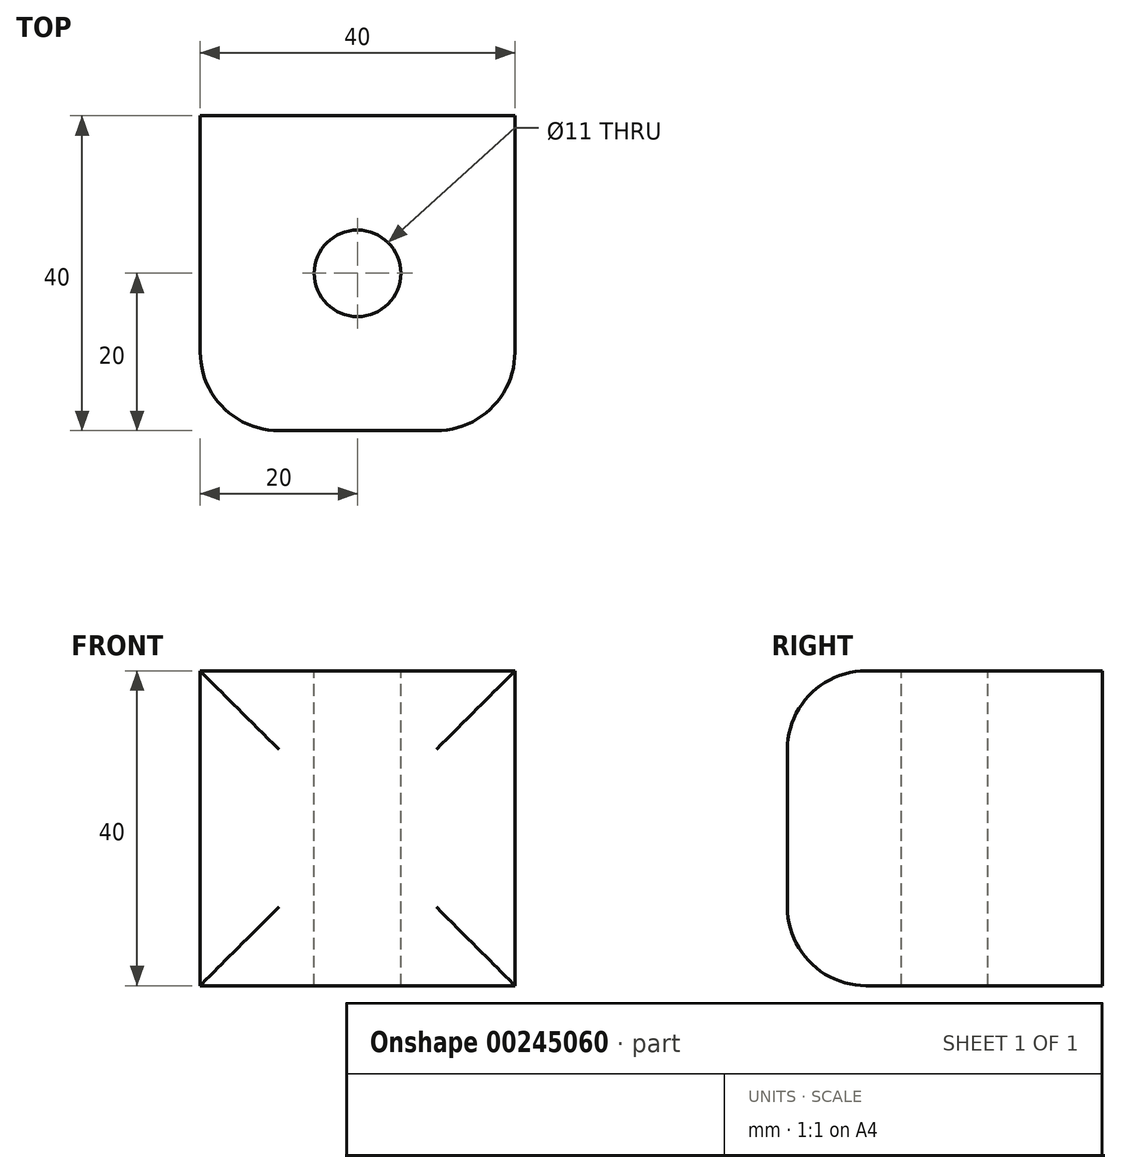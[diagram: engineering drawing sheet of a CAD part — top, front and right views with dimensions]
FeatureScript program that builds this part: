
annotation { "Feature Type Name" : "Feature", "Feature Type Description" : "" }
export const myFeature = defineFeature(function(context is Context, id is Id, definition is map)
    precondition{}
    {
        {
            var Q0;
            Q0=qCreatedBy(makeId("Top.planeOp"),FACE);
            var sketch = newSketch(context, id + "F0", { "sketchPlane" : qUnion([Q0])});
            skLineSegment(sketch, "E0.bottom", {"start": v(-20, 20) * mm, "end": v(20, 20) * mm});
            skLineSegment(sketch, "E0.top", {"start": v(-20, -20) * mm, "end": v(20, -20) * mm});
            skLineSegment(sketch, "E0.left", {"start": v(-20, 20) * mm, "end": v(-20, -20) * mm});
            skLineSegment(sketch, "E0.right", {"start": v(20, 20) * mm, "end": v(20, -20) * mm});
            skPoint(sketch, "E0.middle", {"position": v(0, 0) * mm});
            skSolve(sketch);
        }
        {
            var Q0;
            Q0 = qSketchRegion(id + "F0", true);
            extrude(context, id + "F1", {"entities" : qUnion([Q0]), "depth" : 20 * mm, "hasSecondDirection" : true, "secondDirectionOppositeDirection" : true, "secondDirectionDepth" : 20 * mm});
        }
        {
            var Q0;
            Q0=makeQuery(id+"F1.opExtrude","CAP_FACE",FACE,{"disambiguationData":[OSD([sQuery(id+"F0.wireOp",EDGE,"E0.bottom"),sQuery(id+"F0.wireOp",EDGE,"E0.top"),sQuery(id+"F0.wireOp",EDGE,"E0.left"),sQuery(id+"F0.wireOp",EDGE,"E0.right")])],"isStart":false});
            var sketch = newSketch(context, id + "F2", { "sketchPlane" : qUnion([Q0])});
            skCircle(sketch, "E1", {"center": v(0, 0) * mm, "radius": 5.5 * mm});
            skSolve(sketch);
        }
        {
            var Q0;
            Q0=sQuery(id+"F2.wireOp",VERTEX,"E1.center");
            var Q1;
            Q1=makeQuery(id+"F1.opExtrude","SWEPT_BODY",BODY,{"disambiguationData":[OSD([sQuery(id+"F0.wireOp",EDGE,"E0.bottom"),sQuery(id+"F0.wireOp",EDGE,"E0.top"),sQuery(id+"F0.wireOp",EDGE,"E0.left"),sQuery(id+"F0.wireOp",EDGE,"E0.right")])]});
            hole(context, id + "F3", {"style" : HoleStyle.SIMPLE, "endStyle" : HoleEndStyle.THROUGH, "standardTappedOrClearance" : lookupTablePath({ "standard" : "ISO", "fit" : "Normal", "size" : "M10", "type" : "Clearance" }), "standardBlindInLast" : lookupTablePath({ "fit" : "Standard", "standard" : "ISO", "size" : "M10", "type" : "Clearance" }), "holeDiameter" : 11 * mm, "tappedDepth" : 12 * mm, "tapClearance" : 3, "locations" : qUnion([Q0]), "scope" : qUnion([Q1])});
        }
        {
            var Q0;
            Q0=makeQuery(id+"F1.opExtrude","CAP_EDGE",EDGE,{"disambiguationData":[OSD([sQuery(id+"F0.wireOp",EDGE,"E0.top")])],"isStart":true});
            var Q1;
            Q1=makeQuery(id+"F1.opExtrude","SWEPT_EDGE",EDGE,{"disambiguationData":[OSD([sQuery(id+"F0.wireOp",EDGE,"E0.top"),sQuery(id+"F0.wireOp",EDGE,"E0.right")])]});
            var Q2;
            Q2=makeQuery(id+"F1.opExtrude","SWEPT_EDGE",EDGE,{"disambiguationData":[OSD([sQuery(id+"F0.wireOp",EDGE,"E0.top"),sQuery(id+"F0.wireOp",EDGE,"E0.left")])]});
            var Q3;
            Q3=makeQuery(id+"F1.opExtrude","CAP_EDGE",EDGE,{"disambiguationData":[OSD([sQuery(id+"F0.wireOp",EDGE,"E0.top")])],"isStart":false});
            fillet(context, id + "F4", {"entities" : qUnion([Q0, Q1, Q2, Q3]), "radius" : 10 * mm, "tangentPropagation" : true, "allowEdgeOverflow" : false});
        }
    });
